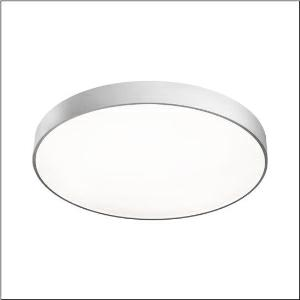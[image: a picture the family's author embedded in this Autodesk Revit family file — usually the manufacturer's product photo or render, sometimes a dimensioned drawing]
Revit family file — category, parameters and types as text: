
# Revit family: round_21_l_51mr38fd0421s
name_source: partatom
category: Lighting Fixtures
units: mm (PartAtom-declared; Revit-internal decimal feet)

## family parameters
Cut with Voids When Loaded = No
Host = Face
Light Source = No
Part Type = Normal
Room Calculation Point = No
Round Connector Dimension = Use Diameter
Shared = No

## types (1)
- Round 21 L (1 x LED, 14150 lm, 97 W, 4000K)
    Apparent Load = 97 VA
    CIE Flux Codes = 49 80 96 100 100
    Color Rendering = 80
    Color Temperature = 4000K
    Default Elevation = 1800 mm
    Description = Round 21 L, wall and ceiling luminaire, primary optical cover: cover, of PMMA, opal, light emission: direct distribution, primary light characteristic: symmetric, installation type: suspended mounting, surface-mounted, LED, rated luminous flux: 13.080lm, luminous efficacy: 146lm/W, light colour: 840, colour temperature: 4000K, control gear: DALI 2, with terminal, 5-pole, mains connection: 230V, AC, 50/60Hz, rated input power: 97W, housing, of aluminium, coated, silver, diameter: 850mm, height: 62mm, protection rating (complete): IP40, insulation class (complete): insulation class I (protective earthing), certification: CE, impact resistance: IK04, permissible operating ambient temperature: -10..+35°C, packaging unit: 1 piece
    Height = 87 mm
    Lamp = 1 x LED
    Lamp Light Flux = 14150 lm
    Lamp Power = 97 W
    Lamp count = 1
    Length = 850 mm
    Luminous efficacy = 146 lm/W
    Manufacturer = Siteco
    ModVariant = No
    Model = 51MR38FD0421S
    Mounting Place = Ceiling
    Mounting Type = Surface mounted
    Number of Poles = 1
    OnlyDefault = Yes
    Power Factor = 1
    Product Name = Round 21 L
    Product group = wall and ceiling luminaire | ceiling mounted
    ProductGroupID = 304
    Protection Class = Protection class I
    Protection Degree = IP 40
    RLX_Detail_Level = 1
    RLX_Emergency_Light_Flux = 0 lm
    RLX_Emergency_Type = 0
    RLX_Emergency_Type_DB = No
    RlxData = <blob elided: 20245 chars, md5=84380c7a>
    Socket = socket
    Standby Power = 0 W
    System Light Flux = 14150 lm
    System Power = 97 W
    Type Comments = Product without accessories
    Type Image = l_1258324.jpg
    URL = http://relux.com
    VarID = ---
    Voltage = 0 V
    Weight = 0.00 kg
    Width = 0 mm  [stored 0 ft]

note: [stored X ft] marks values corroborated as IEEE doubles in the binary element streams (Revit-internal decimal feet)

## geometry (parser evidence)
native form markers: Blend x4, Sweep x9
no freeform markers — native parametric forms only
